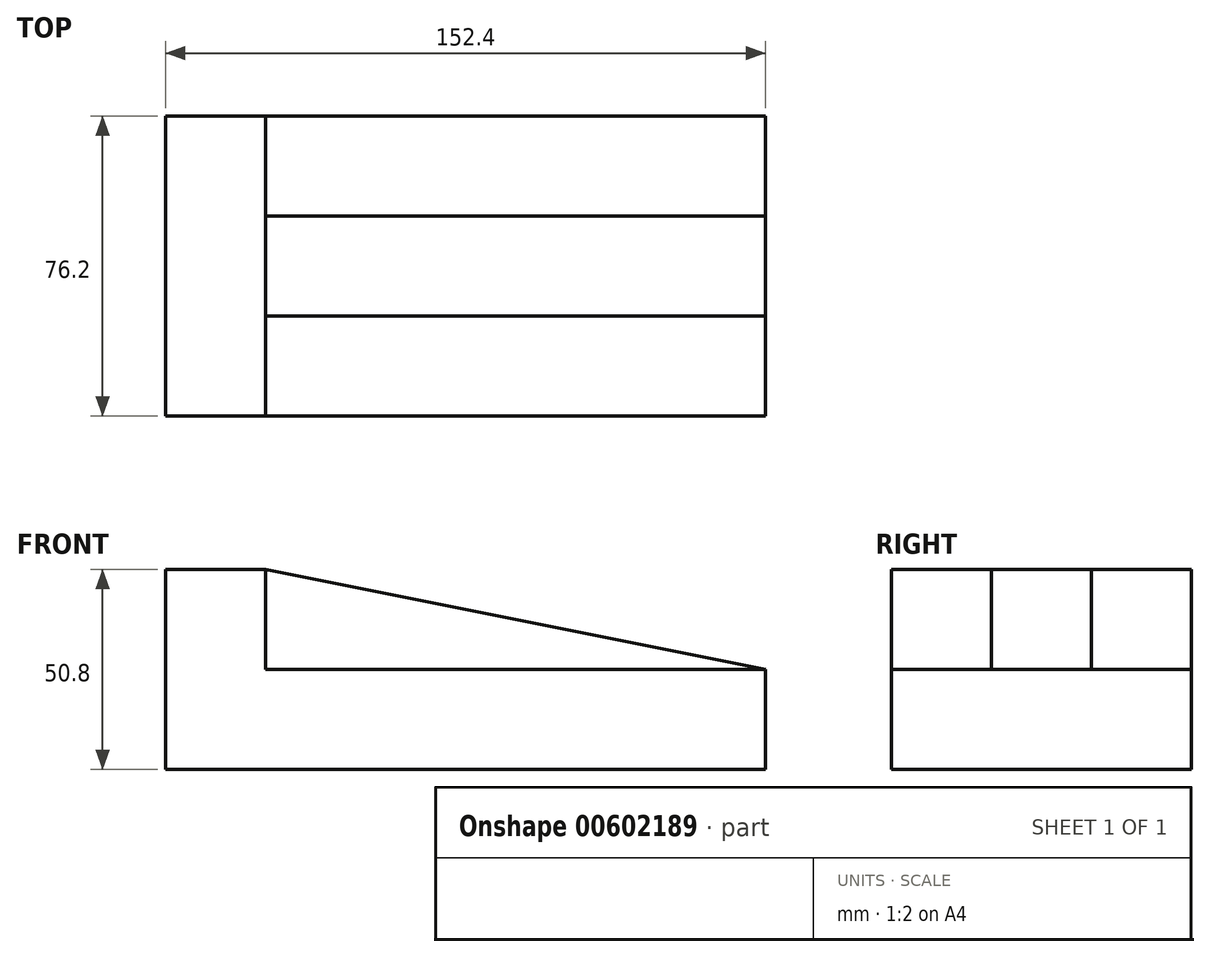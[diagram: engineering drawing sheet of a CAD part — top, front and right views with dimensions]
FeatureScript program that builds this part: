
annotation { "Feature Type Name" : "Feature", "Feature Type Description" : "" }
export const myFeature = defineFeature(function(context is Context, id is Id, definition is map)
    precondition{}
    {
        {
            var Q0;
            Q0=qCreatedBy(makeId("Front.planeOp"),FACE);
            var sketch = newSketch(context, id + "F0", { "sketchPlane" : qUnion([Q0])});
            skLineSegment(sketch, "E0.bottom", {"start": v(104.9, 0) * mm, "end": v(257.3, 0) * mm});
            skLineSegment(sketch, "E0.top", {"start": v(104.9, 50.8) * mm, "end": v(130.3, 50.8) * mm});
            skLineSegment(sketch, "E0.left", {"start": v(104.9, 0) * mm, "end": v(104.9, 50.8) * mm});
            skLineSegment(sketch, "E0.right", {"start": v(257.3, 0) * mm, "end": v(257.3, 25.4) * mm});
            skLineSegment(sketch, "E1", {"start": v(130.3, 50.8) * mm, "end": v(130.3, 25.4) * mm});
            skLineSegment(sketch, "E2", {"start": v(130.3, 25.4) * mm, "end": v(257.3, 25.4) * mm});
            skLineSegment(sketch, "E3", {"start": v(130.3, 50.8) * mm, "end": v(257.3, 25.4) * mm});
            skPoint(sketch, "E4.orphan", {"position": v(257.3, 50.8) * mm});
            skSolve(sketch);
        }
        {
            var Q0;
            Q0=makeQuery(id+"F0.imprint","IMPRINT",FACE,{"disambiguationData":[TD([[makeQuery(id+"F0.imprint","IMPRINT",EDGE,{"derivedFrom":sQuery(id+"F0.wireOp",EDGE,"E0.bottom")}),1.0]])]});
            extrude(context, id + "F1", {"entities" : qUnion([Q0]), "oppositeDirection" : true, "depth" : 76.2 * mm, "offsetDistance" : 25.4 * mm});
        }
        {
            var Q0;
            Q0=makeQuery(id+"F1.opExtrude","SWEPT_FACE",FACE,{"disambiguationData":[OSD([sQuery(id+"F0.wireOp",EDGE,"E2")])]});
            var sketch = newSketch(context, id + "F2", { "sketchPlane" : qUnion([Q0])});
            skLineSegment(sketch, "E5", {"start": v(130.3, 76.2) * mm, "end": v(130.3, 50.8) * mm});
            skLineSegment(sketch, "E6", {"start": v(130.3, 0) * mm, "end": v(130.3, 25.4) * mm});
            skLineSegment(sketch, "E7", {"start": v(130.3, 25.4) * mm, "end": v(257.3, 25.4) * mm});
            skLineSegment(sketch, "E8", {"start": v(130.3, 50.8) * mm, "end": v(257.3, 50.8) * mm});
            skSolve(sketch);
        }
        {
            var Q0;
            {var subQ0=sQuery(id+"F2.wireOp",EDGE,"E7");Q0=makeQuery(id+"F2.imprint","IMPRINT",FACE,{"disambiguationData":[TD([[makeQuery(id+"F2.imprint","IMPRINT",EDGE,{"derivedFrom":subQ0}),1.0]])]});}
            extrude(context, id + "F3", {"entities" : qUnion([Q0]), "operationType" : NewBodyOperationType.ADD, "depth" : 25.4 * mm, "offsetDistance" : 25.4 * mm});
        }
        {
            var Q0;
            Q0=makeQuery(id+"F3.opExtrude","SWEPT_FACE",FACE,{"disambiguationData":[OSD([sQuery(id+"F2.wireOp",EDGE,"E7")])]});
            var sketch = newSketch(context, id + "F4", { "sketchPlane" : qUnion([Q0])});
            skLineSegment(sketch, "E9", {"start": v(130.3, 50.8) * mm, "end": v(257.3, 25.4) * mm});
            skSolve(sketch);
        }
        {
            var Q0;
            Q0=makeQuery(id+"F4.imprint","IMPRINT",FACE,{"disambiguationData":[TD([[makeQuery(id+"F4.imprint","IMPRINT",EDGE,{"derivedFrom":sQuery(id+"F4.wireOp",EDGE,"E9")}),1.0]])]});
            extrude(context, id + "F5", {"entities" : qUnion([Q0]), "operationType" : NewBodyOperationType.REMOVE, "oppositeDirection" : true, "depth" : 25.4 * mm, "offsetDistance" : 25.4 * mm});
        }
    });
